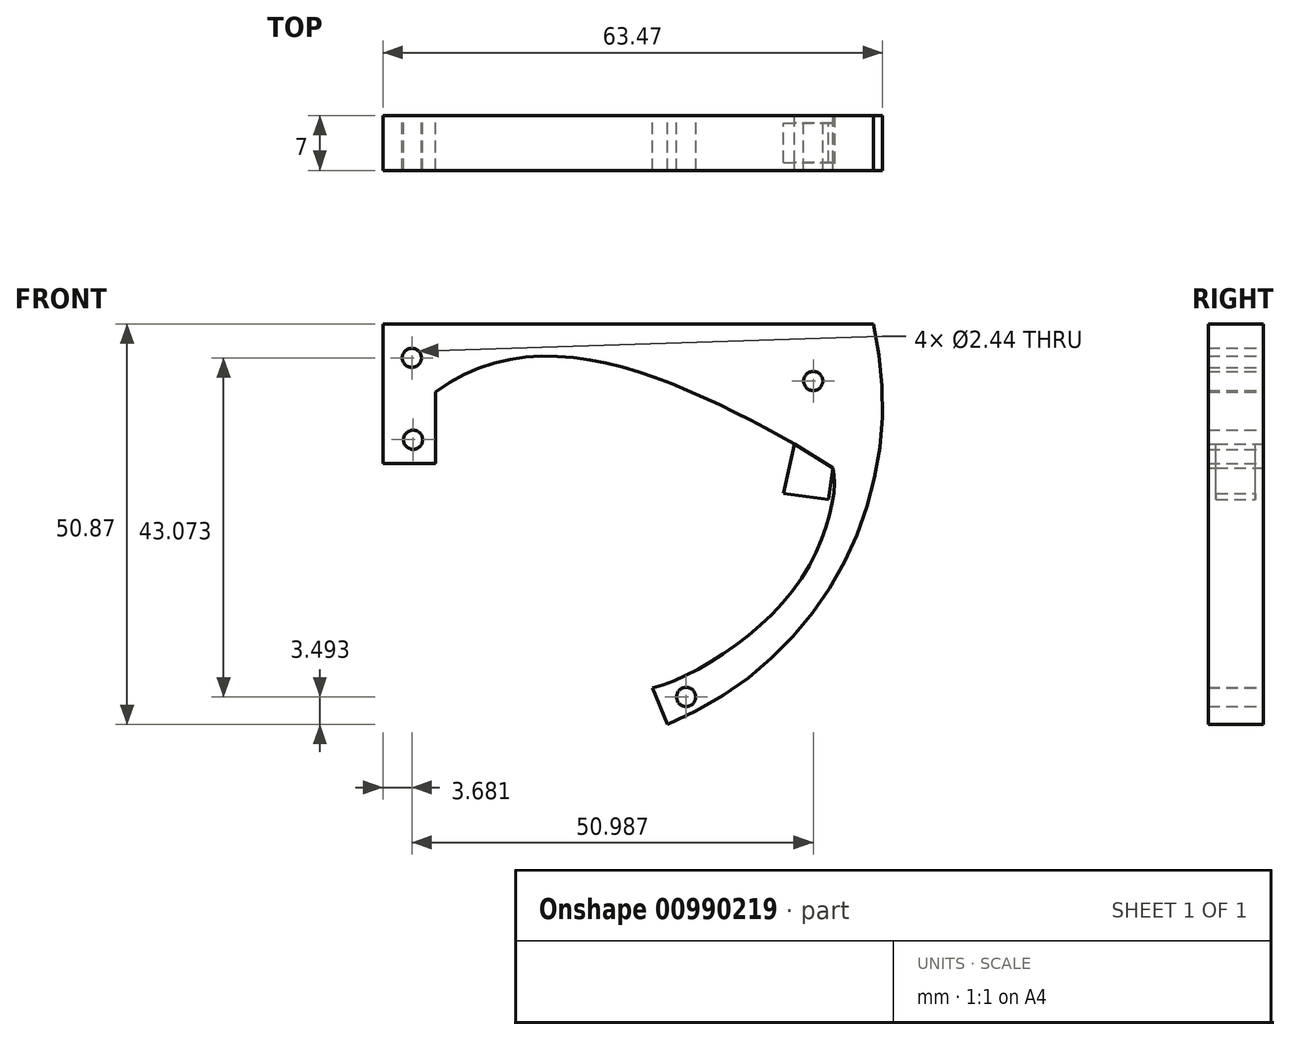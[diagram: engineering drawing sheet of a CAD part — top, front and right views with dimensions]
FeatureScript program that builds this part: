
annotation { "Feature Type Name" : "Feature", "Feature Type Description" : "" }
export const myFeature = defineFeature(function(context is Context, id is Id, definition is map)
    precondition{}
    {
        {
            var Q0;
            Q0=qCreatedBy(makeId("Front.planeOp"),FACE);
            var sketch = newSketch(context, id + "F0", { "sketchPlane" : qUnion([Q0])});
            skLineSegment(sketch, "E0", {"start": v(0, 21.44) * mm, "end": v(62.3, 21.44) * mm});
            skLineSegment(sketch, "E1", {"start": v(34.27, -24.8) * mm, "end": v(36.14, -29.43) * mm});
            skArc(sketch, "E2", {"start": v(36.14, -29.43) * mm, "mid": v(58.6, -8.82) * mm, "end": v(62.3, 21.44) * mm});
            skCircle(sketch, "E3", {"center": v(3.68, 17.14) * mm, "radius": 1.22 * mm});
            skCircle(sketch, "E4", {"center": v(3.84, 6.74) * mm, "radius": 1.22 * mm});
            skCircle(sketch, "E5", {"center": v(54.67, 14.2) * mm, "radius": 1.22 * mm});
            skCircle(sketch, "E6", {"center": v(38.52, -25.94) * mm, "radius": 1.22 * mm});
            skCircle(sketch, "E7", {"center": v(19.82, 11.13) * mm, "radius": 1.22 * mm});
            skLineSegment(sketch, "E8", {"start": v(0, 21.44) * mm, "end": v(0, 3.73) * mm});
            skLineSegment(sketch, "E9", {"start": v(0, 3.73) * mm, "end": v(6.67, 3.73) * mm});
            skLineSegment(sketch, "E10", {"start": v(6.67, 3.73) * mm, "end": v(6.67, 12.79) * mm});
            skFitSpline(sketch, "E11", {"points": [v(34.27, -24.8) * mm, v(52.85, -11.37) * mm, v(57.14, 3.16) * mm], "startDerivative": vector(28.58, 7.3) * mm, "endDerivative": vector(-4.8, 17.89) * mm});
            skLineSegment(sketch, "E12", {"start": v(57.14, 3.16) * mm, "end": v(52.3, 6.17) * mm});
            skFitSpline(sketch, "E13", {"points": [v(6.67, 12.79) * mm, v(52.3, 6.17) * mm], "startDerivative": vector(41.09, 30.77) * mm, "endDerivative": vector(41.7, -23.1) * mm});
            skLineSegment(sketch, "E14", {"start": v(50.91, -0.1) * mm, "end": v(56.6, -0.85) * mm});
            skLineSegment(sketch, "E15", {"start": v(56.6, -0.85) * mm, "end": v(57.14, 3.16) * mm});
            skLineSegment(sketch, "E16", {"start": v(50.91, -0.1) * mm, "end": v(52.3, 6.17) * mm});
            skLineSegment(sketch, "E17", {"start": v(53.76, -0.47) * mm, "end": v(54.72, 4.67) * mm});
            skSolve(sketch);
        }
        {
            var Q0;
            Q0=makeQuery(id+"F0.imprint","IMPRINT",FACE,{"disambiguationData":[TD([[makeQuery(id+"F0.imprint","IMPRINT",EDGE,{"derivedFrom":sQuery(id+"F0.wireOp",EDGE,"E0")}),-1.0]])]});
            extrude(context, id + "F1", {"entities" : qUnion([Q0]), "endBound" : BoundingType.SYMMETRIC, "depth" : 7 * mm, "offsetDistance" : 25 * mm});
        }
        {
            var Q0;
            {var subQ0=sQuery(id+"F0.wireOp",EDGE,"E16");Q0=makeQuery(id+"F0.imprint","IMPRINT",FACE,{"disambiguationData":[TD([[makeQuery(id+"F0.imprint","IMPRINT",EDGE,{"derivedFrom":subQ0}),-1.0]])]});}
            var Q1;
            {var subQ0=sQuery(id+"F0.wireOp",EDGE,"E15");Q1=makeQuery(id+"F0.imprint","IMPRINT",FACE,{"disambiguationData":[TD([[makeQuery(id+"F0.imprint","IMPRINT",EDGE,{"derivedFrom":subQ0}),1.0]])]});}
            extrude(context, id + "F2", {"entities" : qUnion([Q0, Q1]), "operationType" : NewBodyOperationType.ADD, "endBound" : BoundingType.SYMMETRIC, "depth" : 5 * mm, "offsetDistance" : 25 * mm});
        }
    });
